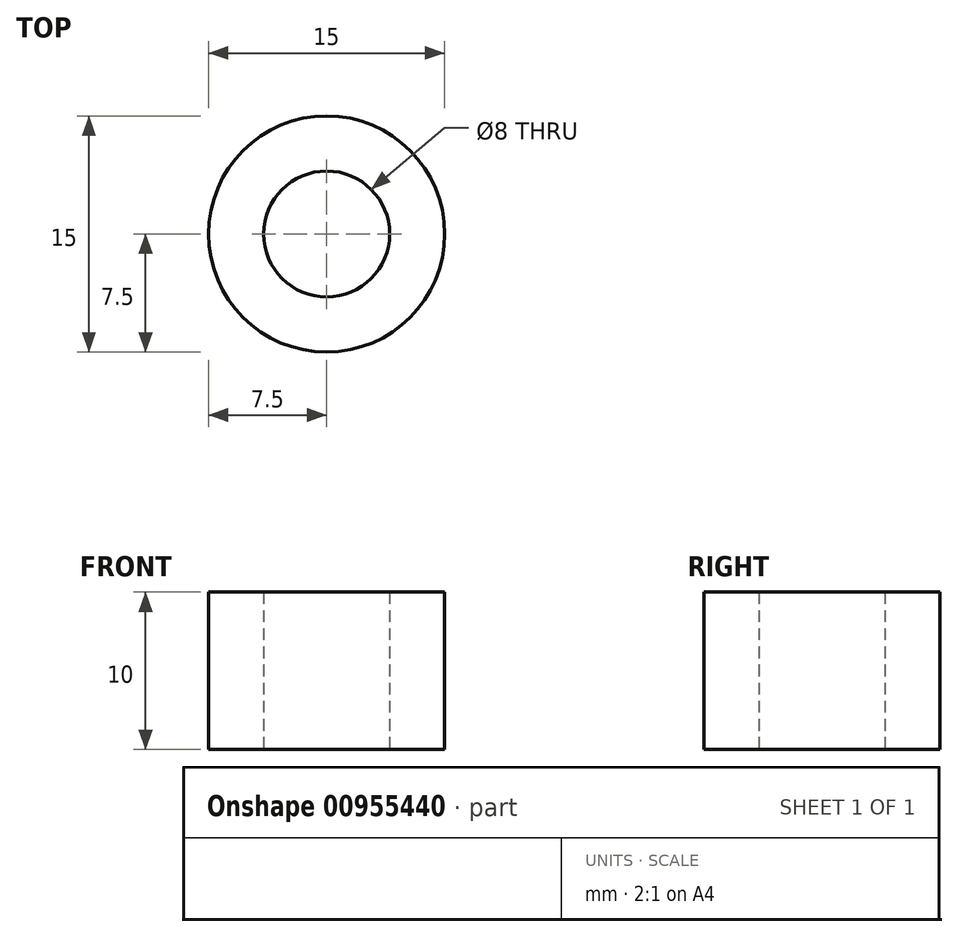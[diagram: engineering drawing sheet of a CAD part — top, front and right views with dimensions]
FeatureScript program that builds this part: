
annotation { "Feature Type Name" : "Feature", "Feature Type Description" : "" }
export const myFeature = defineFeature(function(context is Context, id is Id, definition is map)
    precondition{}
    {
        {
            var Q0;
            Q0=qCreatedBy(makeId("Top.planeOp"),FACE);
            var sketch = newSketch(context, id + "F0", { "sketchPlane" : qUnion([Q0])});
            skCircle(sketch, "E0", {"center": v(0, 0) * mm, "radius": 7.5 * mm});
            skCircle(sketch, "E1", {"center": v(0, 0) * mm, "radius": 4 * mm});
            skSolve(sketch);
        }
        {
            var Q0;
            Q0=makeQuery(id+"F0.imprint","IMPRINT",FACE,{"disambiguationData":[TD([[makeQuery(id+"F0.imprint","IMPRINT",EDGE,{"derivedFrom":sQuery(id+"F0.wireOp",EDGE,"E0")}),1.0]])]});
            extrude(context, id + "F1", {"entities" : qUnion([Q0]), "depth" : 10 * mm, "offsetDistance" : 25 * mm});
        }
        {
            var Q0;
            Q0=qCreatedBy(makeId("Front.planeOp"),FACE);
            var sketch = newSketch(context, id + "F2", { "sketchPlane" : qUnion([Q0])});
            skLineSegment(sketch, "E2.bottom", {"start": v(16.17, 42.66) * mm, "end": v(46.17, 42.66) * mm});
            skLineSegment(sketch, "E2.top", {"start": v(16.17, 41.66) * mm, "end": v(46.17, 41.66) * mm});
            skLineSegment(sketch, "E2.left", {"start": v(16.17, 42.66) * mm, "end": v(16.17, 41.66) * mm});
            skLineSegment(sketch, "E2.right", {"start": v(46.17, 42.66) * mm, "end": v(46.17, 41.66) * mm});
            skSolve(sketch);
        }
        {
            var Q0;
            Q0=makeQuery(id+"F2.imprint","IMPRINT",FACE,{"disambiguationData":[TD([[makeQuery(id+"F2.imprint","IMPRINT",EDGE,{"derivedFrom":sQuery(id+"F2.wireOp",EDGE,"E2.bottom")}),-1.0]])]});
            var Q1;
            Q1=sQuery(id+"F2.wireOp",EDGE,"E2.bottom");
            revolve(context, id + "F3", {"surfaceOperationType" : NewSurfaceOperationType.NEW, "entities" : qUnion([Q0]), "axis" : qUnion([Q1]), "revolveType" : RevolveType.FULL});
        }
        {
            var Q0;
            Q0=makeQuery(id+"F3.opRevolve","SWEPT_BODY",BODY,{"disambiguationData":[OSD([sQuery(id+"F2.wireOp",EDGE,"E2.bottom"),sQuery(id+"F2.wireOp",EDGE,"E2.top"),sQuery(id+"F2.wireOp",EDGE,"E2.left"),sQuery(id+"F2.wireOp",EDGE,"E2.right")])]});
            deleteBodies(context, id + "F4", {"entities" : qUnion([Q0])});
        }
    });
